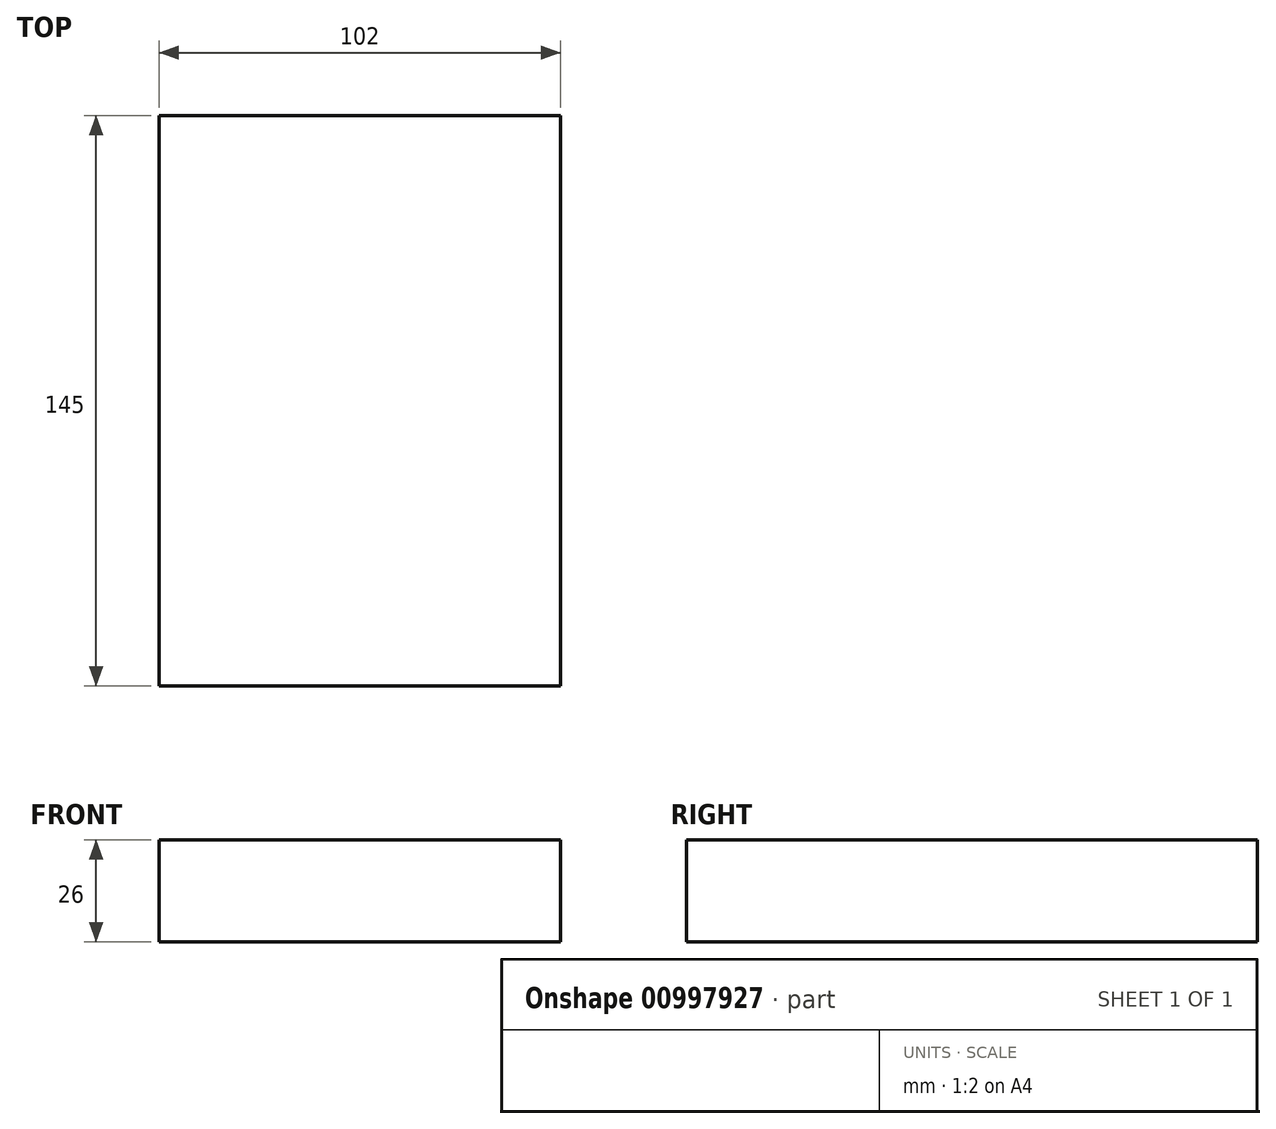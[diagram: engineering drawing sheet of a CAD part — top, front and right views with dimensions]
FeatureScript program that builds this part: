
annotation { "Feature Type Name" : "Feature", "Feature Type Description" : "" }
export const myFeature = defineFeature(function(context is Context, id is Id, definition is map)
    precondition{}
    {
        {
            var Q0;
            Q0=qCreatedBy(makeId("Top.planeOp"),FACE);
            var sketch = newSketch(context, id + "F0", { "sketchPlane" : qUnion([Q0])});
            skLineSegment(sketch, "E0.bottom", {"start": v(51, -72.5) * mm, "end": v(-51, -72.5) * mm});
            skLineSegment(sketch, "E0.top", {"start": v(51, 72.5) * mm, "end": v(-51, 72.5) * mm});
            skLineSegment(sketch, "E0.left", {"start": v(51, -72.5) * mm, "end": v(51, 72.5) * mm});
            skLineSegment(sketch, "E0.right", {"start": v(-51, -72.5) * mm, "end": v(-51, 72.5) * mm});
            skPoint(sketch, "E0.middle", {"position": v(0, 0) * mm});
            skSolve(sketch);
        }
        {
            var Q0;
            Q0=makeQuery(id+"F0.imprint","IMPRINT",FACE,{"disambiguationData":[TD([[makeQuery(id+"F0.imprint","IMPRINT",EDGE,{"derivedFrom":sQuery(id+"F0.wireOp",EDGE,"E0.bottom")}),-1.0]])]});
            extrude(context, id + "F1", {"entities" : qUnion([Q0]), "depth" : 26 * mm, "offsetDistance" : 25 * mm});
        }
    });
